# Revit family: a
name_source: partatom
category: Doors
revit_build: Autodesk Revit 2018 (Build: 20181011_1500(x64)
units: mm (PartAtom-declared; Revit-internal decimal feet)

## family parameters
Cut with Voids When Loaded = No
Host = Face
OmniClass Number = 23.30.10.27.17
OmniClass Title = Access Doors
Room Calculation Point = No
Shared = No

## types (1)
- (See Type Catalog)
    Arm Guide GAP = 0"
    Arm Guide Location = 4 3/4"
    Cover Length = 76 5/8"
    Cover Material = Steel-Bilco-Red Oxide Primer Finish
    Cover Opening = 90.00°
    Cover Overlap = 2 5/16"
    Cover Type = Cover-Bilco-With_1in_Pan_to_Receive_Flooring_Material_150_PSF
    Cover Width = 52 5/8"
    Default Elevation = 48"
    Description = Floor Access Door
    Flooring Material = <By Category>
    Frame Material = Steel-Bilco-Red Oxide Primer Finish
    Frame Type = Frame-Bilco-Non_Drainage_Channel_Frame_2_Double
    Function = Interior
    Hardware Material = Stainless Steel-Bilco-316
    Has Arm Guide 1 = No
    Has Arm Guide 2 = Yes
    Has Double Lifting Mechanism = Yes
    Has Single Lifting Mechanism = Yes
    Has Support Shelf = No
    Has Tile Ending = No
    Height = 12 19/32"
    Length = 72"
    Lifting Mechanism Connector = Lifting_Mechanism-Bilco-Special_Connector : By Type
    Lifting Mechanism Location = 5 1/8"
    Manufacturer = Bilco
    Rough Difference = 3"
    Rough Height = 78"
    Rough Width = 54"
    Spring Tube Material = Brass-Bilco-Satin
    URL = http://www.bilco.com
    Width = 48"

## geometry (parser evidence)
native form markers: Blend x20, Sweep x53
no freeform markers — native parametric forms only
